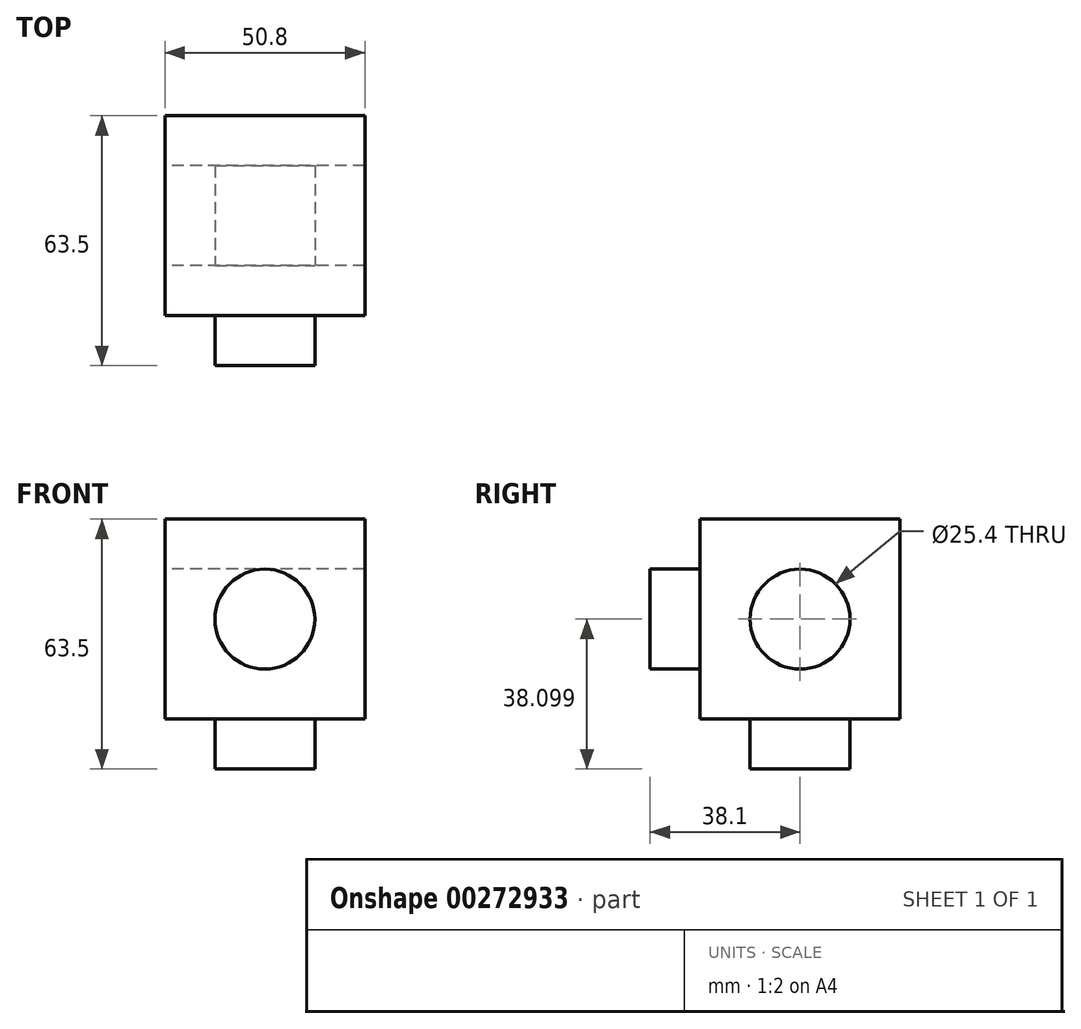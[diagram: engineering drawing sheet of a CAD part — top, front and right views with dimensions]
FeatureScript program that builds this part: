
annotation { "Feature Type Name" : "Feature", "Feature Type Description" : "" }
export const myFeature = defineFeature(function(context is Context, id is Id, definition is map)
    precondition{}
    {
        {
            var Q0;
            Q0=qCreatedBy(makeId("Front.planeOp"),FACE);
            var sketch = newSketch(context, id + "F0", { "sketchPlane" : qUnion([Q0])});
            skLineSegment(sketch, "E0.bottom", {"start": v(-50.8, 46.6) * mm, "end": v(0, 46.6) * mm});
            skLineSegment(sketch, "E0.top", {"start": v(-50.8, -4.2) * mm, "end": v(0, -4.2) * mm});
            skLineSegment(sketch, "E0.left", {"start": v(-50.8, 46.6) * mm, "end": v(-50.8, -4.2) * mm});
            skLineSegment(sketch, "E0.right", {"start": v(0, 46.6) * mm, "end": v(0, -4.2) * mm});
            skSolve(sketch);
        }
        {
            var Q0;
            Q0 = qSketchRegion(id + "F0", true);
            extrude(context, id + "F1", {"entities" : qUnion([Q0]), "depth" : 50.8 * mm});
        }
        {
            var Q0;
            Q0=makeQuery(id+"F1.opExtrude","CAP_FACE",FACE,{"disambiguationData":[OSD([sQuery(id+"F0.wireOp",EDGE,"E0.bottom"),sQuery(id+"F0.wireOp",EDGE,"E0.top"),sQuery(id+"F0.wireOp",EDGE,"E0.left"),sQuery(id+"F0.wireOp",EDGE,"E0.right")])],"isStart":false});
            var sketch = newSketch(context, id + "F2", { "sketchPlane" : qUnion([Q0])});
            skCircle(sketch, "E1", {"center": v(-25.4, 21.2) * mm, "radius": 12.7 * mm});
            skSolve(sketch);
        }
        {
            var Q0;
            Q0 = qSketchRegion(id + "F2", true);
            extrude(context, id + "F3", {"entities" : qUnion([Q0]), "operationType" : NewBodyOperationType.ADD, "depth" : 12.7 * mm});
        }
        {
            var Q0;
            Q0=makeQuery(id+"F1.opExtrude","SWEPT_FACE",FACE,{"disambiguationData":[OSD([sQuery(id+"F0.wireOp",EDGE,"E0.left")])]});
            var sketch = newSketch(context, id + "F4", { "sketchPlane" : qUnion([Q0])});
            skCircle(sketch, "E2", {"center": v(25.4, 21.2) * mm, "radius": 12.7 * mm});
            skSolve(sketch);
        }
        {
            var Q0;
            Q0 = qSketchRegion(id + "F4", true);
            extrude(context, id + "F5", {"entities" : qUnion([Q0]), "operationType" : NewBodyOperationType.REMOVE, "oppositeDirection" : true, "depth" : 50.8 * mm});
        }
        {
            var Q0;
            Q0=makeQuery(id+"F1.opExtrude","SWEPT_FACE",FACE,{"disambiguationData":[OSD([sQuery(id+"F0.wireOp",EDGE,"E0.top")])]});
            var sketch = newSketch(context, id + "F6", { "sketchPlane" : qUnion([Q0])});
            skLineSegment(sketch, "E3.bottom", {"start": v(-38.1, 12.7) * mm, "end": v(-12.7, 12.7) * mm});
            skLineSegment(sketch, "E3.top", {"start": v(-38.1, 38.1) * mm, "end": v(-12.7, 38.1) * mm});
            skLineSegment(sketch, "E3.left", {"start": v(-38.1, 12.7) * mm, "end": v(-38.1, 38.1) * mm});
            skLineSegment(sketch, "E3.right", {"start": v(-12.7, 12.7) * mm, "end": v(-12.7, 38.1) * mm});
            skSolve(sketch);
        }
        {
            var Q0;
            Q0 = qSketchRegion(id + "F6", true);
            extrude(context, id + "F7", {"entities" : qUnion([Q0]), "operationType" : NewBodyOperationType.ADD, "depth" : 12.7 * mm});
        }
    });
